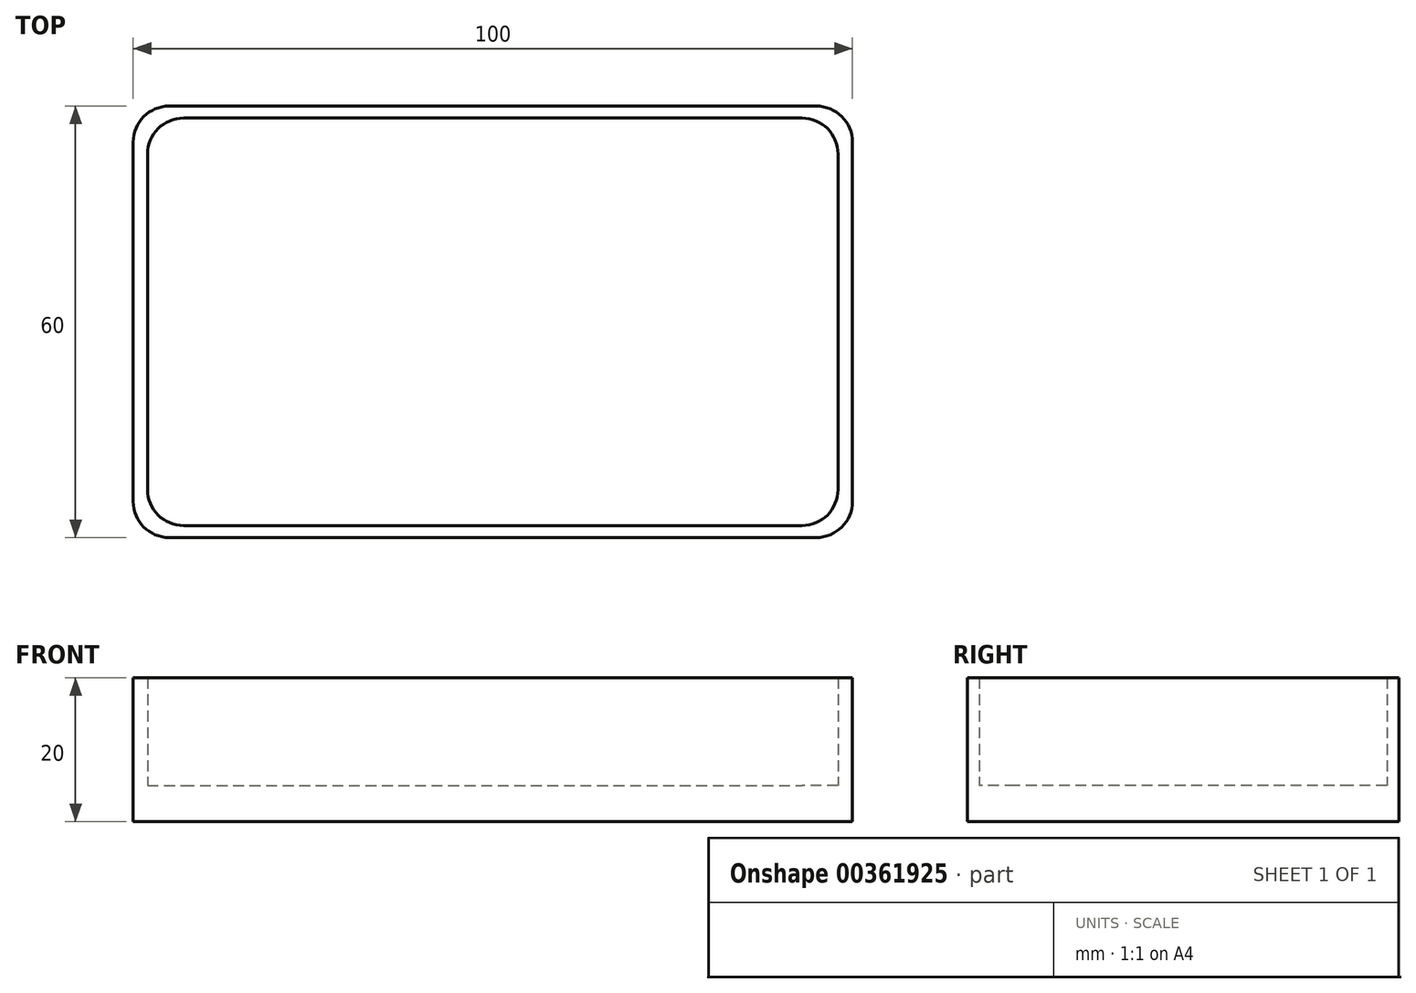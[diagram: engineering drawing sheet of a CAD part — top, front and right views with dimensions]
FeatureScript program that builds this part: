
annotation { "Feature Type Name" : "Feature", "Feature Type Description" : "" }
export const myFeature = defineFeature(function(context is Context, id is Id, definition is map)
    precondition{}
    {
        {
            var Q0;
            Q0=qCreatedBy(makeId("Top.planeOp"),FACE);
            var sketch = newSketch(context, id + "F0", { "sketchPlane" : qUnion([Q0])});
            skPoint(sketch, "E0.middle", {"position": v(0, 0) * mm});
            skLineSegment(sketch, "E1.bottom", {"start": v(45, -30) * mm, "end": v(-45, -30) * mm});
            skLineSegment(sketch, "E1.top", {"start": v(45, 30) * mm, "end": v(-45, 30) * mm});
            skLineSegment(sketch, "E1.left", {"start": v(50, -25) * mm, "end": v(50, 25) * mm});
            skLineSegment(sketch, "E1.right", {"start": v(-50, -25) * mm, "end": v(-50, 25) * mm});
            skLineSegment(sketch, "E2.bottom", {"start": v(-43, 28.33) * mm, "end": v(43, 28.33) * mm});
            skLineSegment(sketch, "E2.top", {"start": v(-43, -28.33) * mm, "end": v(43, -28.33) * mm});
            skLineSegment(sketch, "E2.left", {"start": v(-48, 23.33) * mm, "end": v(-48, -23.33) * mm});
            skLineSegment(sketch, "E2.right", {"start": v(48, 23.33) * mm, "end": v(48, -23.33) * mm});
            skPoint(sketch, "E3.visualSharp", {"position": v(-48, 28.33) * mm});
            skArc(sketch, "E3.filletArc", {"start": v(-43, 28.33) * mm, "mid": v(-46.54, 26.86) * mm, "end": v(-48, 23.33) * mm});
            skPoint(sketch, "E4.visualSharp", {"position": v(-50, 30) * mm});
            skArc(sketch, "E4.filletArc", {"start": v(-45, 30) * mm, "mid": v(-48.54, 28.54) * mm, "end": v(-50, 25) * mm});
            skPoint(sketch, "E5.visualSharp", {"position": v(-48, -28.33) * mm});
            skArc(sketch, "E5.filletArc", {"start": v(-48, -23.33) * mm, "mid": v(-46.54, -26.86) * mm, "end": v(-43, -28.33) * mm});
            skPoint(sketch, "E6.visualSharp", {"position": v(-50, -30) * mm});
            skArc(sketch, "E6.filletArc", {"start": v(-50, -25) * mm, "mid": v(-48.54, -28.54) * mm, "end": v(-45, -30) * mm});
            skPoint(sketch, "E7.visualSharp", {"position": v(48, -28.33) * mm});
            skArc(sketch, "E7.filletArc", {"start": v(43, -28.33) * mm, "mid": v(46.54, -26.86) * mm, "end": v(48, -23.33) * mm});
            skPoint(sketch, "E8.visualSharp", {"position": v(50, -30) * mm});
            skArc(sketch, "E8.filletArc", {"start": v(45, -30) * mm, "mid": v(48.54, -28.54) * mm, "end": v(50, -25) * mm});
            skPoint(sketch, "E9.visualSharp", {"position": v(50, 30) * mm});
            skArc(sketch, "E9.filletArc", {"start": v(50, 25) * mm, "mid": v(48.54, 28.54) * mm, "end": v(45, 30) * mm});
            skPoint(sketch, "E10.visualSharp", {"position": v(48, 28.33) * mm});
            skArc(sketch, "E10.filletArc", {"start": v(48, 23.33) * mm, "mid": v(46.54, 26.86) * mm, "end": v(43, 28.33) * mm});
            skSolve(sketch);
        }
        {
            var Q0;
            Q0=makeQuery(id+"F0.imprint","IMPRINT",FACE,{"disambiguationData":[TD([[makeQuery(id+"F0.imprint","IMPRINT",EDGE,{"derivedFrom":sQuery(id+"F0.wireOp",EDGE,"E1.bottom")}),-1.0]])]});
            extrude(context, id + "F1", {"entities" : qUnion([Q0]), "depth" : 20 * mm});
        }
        {
            var Q0;
            Q0=makeQuery(id+"F0.imprint","IMPRINT",FACE,{"disambiguationData":[TD([[makeQuery(id+"F0.imprint","IMPRINT",EDGE,{"derivedFrom":sQuery(id+"F0.wireOp",EDGE,"E2.bottom")}),-1.0]])]});
            extrude(context, id + "F2", {"entities" : qUnion([Q0]), "operationType" : NewBodyOperationType.ADD, "depth" : 5 * mm});
        }
    });
